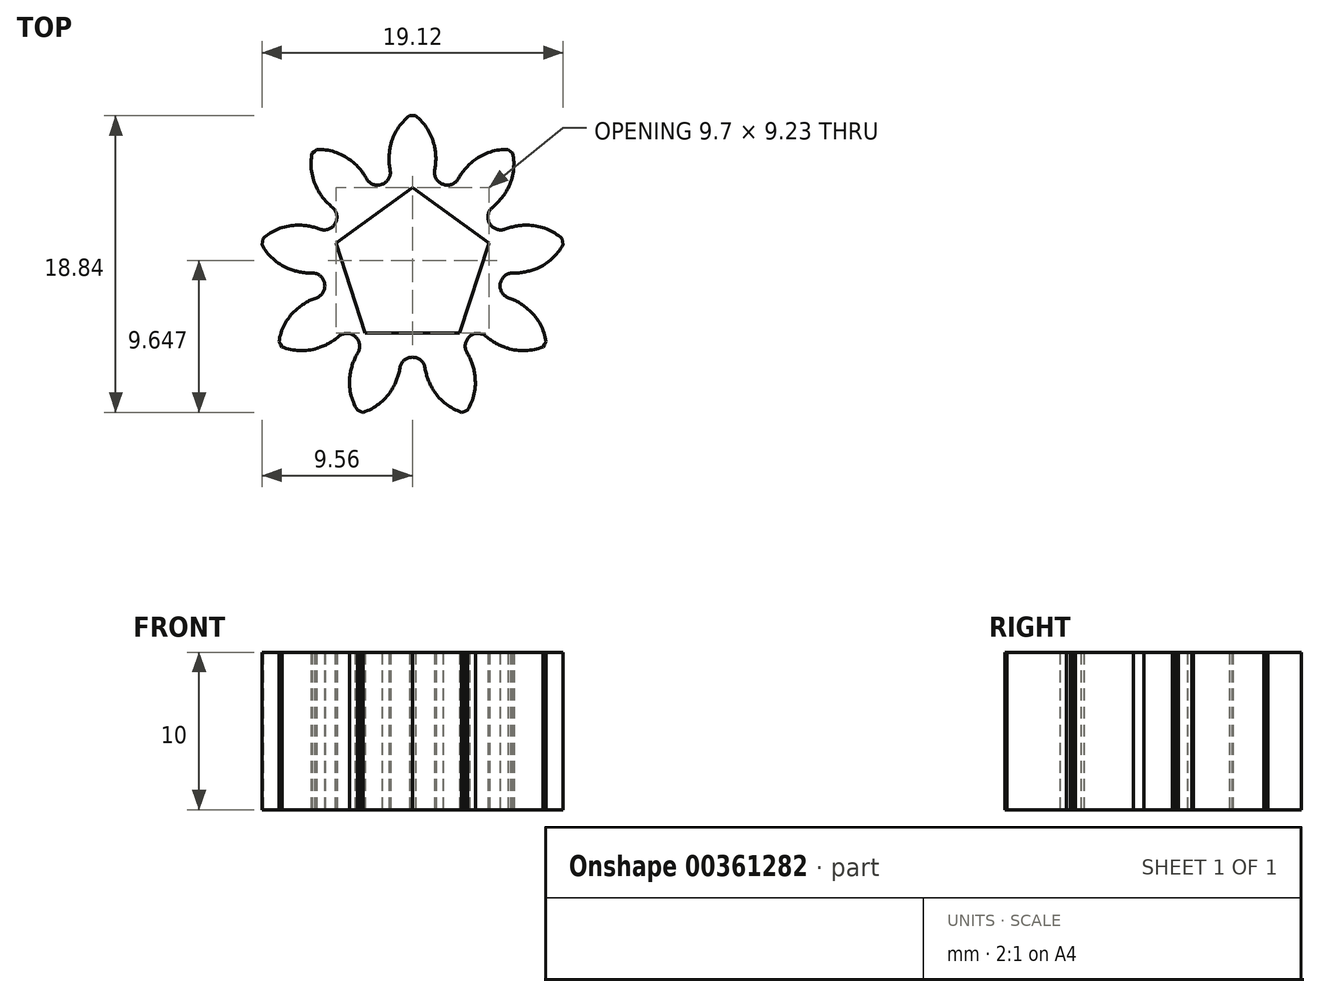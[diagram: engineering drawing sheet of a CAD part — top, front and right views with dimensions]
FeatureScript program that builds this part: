
annotation { "Feature Type Name" : "Feature", "Feature Type Description" : "" }
export const myFeature = defineFeature(function(context is Context, id is Id, definition is map)
    precondition{}
    {
        {
            var Q0;
            Q0=qCreatedBy(makeId("Top.planeOp"),FACE);
            var sketch = newSketch(context, id + "F0", { "sketchPlane" : qUnion([Q0])});
            skCircle(sketch, "E0", {"center": v(0, 0) * mm, "radius": 7.9 * mm, "construction": true});
            skCircle(sketch, "E1", {"center": v(0, 0) * mm, "radius": 9.68 * mm, "construction": true});
            skCircle(sketch, "E2", {"center": v(0, 0) * mm, "radius": 5.68 * mm, "construction": true});
            skLineSegment(sketch, "E3", {"start": v(0, 0) * mm, "end": v(0, 14.6) * mm, "construction": true});
            skLineSegment(sketch, "E4", {"start": v(0, 0) * mm, "end": v(-6.05, 14.6) * mm, "construction": true});
            skLineSegment(sketch, "E5", {"start": v(0, 0) * mm, "end": v(6.05, 14.6) * mm, "construction": true});
            skCircle(sketch, "E6", {"center": v(0, 7.9) * mm, "radius": 1.4 * mm, "construction": true});
            skCircle(sketch, "E7", {"center": v(0, 0) * mm, "radius": 7.3 * mm, "construction": true});
            skCircle(sketch, "E8", {"center": v(1.39, 7.78) * mm, "radius": 3.3 * mm, "construction": true});
            skCircle(sketch, "E9", {"center": v(1.39, 7.78) * mm, "radius": 3.77 * mm, "construction": true});
            skArc(sketch, "E10", {"start": v(1.42, 6.23) * mm, "mid": v(1.48, 7) * mm, "end": v(1.39, 7.78) * mm});
            skArc(sketch, "E11.trimOffspring", {"start": v(1.39, 7.78) * mm, "mid": v(0.96, 8.83) * mm, "end": v(0.19, 9.68) * mm});
            skLineSegment(sketch, "E12", {"start": v(2.17, 5.25) * mm, "end": v(1.96, 5.31) * mm});
            skLineSegment(sketch, "E13", {"start": v(0, 9.68) * mm, "end": v(0.19, 9.68) * mm});
            skPoint(sketch, "E14.visualSharp", {"position": v(1.22, 5.55) * mm});
            skArc(sketch, "E14.filletArc", {"start": v(1.42, 6.23) * mm, "mid": v(1.52, 5.67) * mm, "end": v(1.96, 5.31) * mm});
            skLineSegment(sketch, "E15.MirrorCS", {"start": v(-2.17, 5.25) * mm, "end": v(-1.96, 5.31) * mm});
            skLineSegment(sketch, "E16.MirrorCS", {"start": v(0, 9.68) * mm, "end": v(-0.19, 9.68) * mm});
            skArc(sketch, "E17.MirrorCS", {"start": v(-1.39, 7.78) * mm, "mid": v(-0.96, 8.83) * mm, "end": v(-0.19, 9.68) * mm});
            skArc(sketch, "E18.MirrorCS", {"start": v(-1.42, 6.23) * mm, "mid": v(-1.48, 7) * mm, "end": v(-1.39, 7.78) * mm});
            skArc(sketch, "E19.MirrorCS", {"start": v(-1.42, 6.23) * mm, "mid": v(-1.52, 5.67) * mm, "end": v(-1.96, 5.31) * mm});
            skLineSegment(sketch, "E20.1.0", {"start": v(-5.04, 2.62) * mm, "end": v(-4.92, 2.8) * mm});
            skArc(sketch, "E20.1.1", {"start": v(-5.09, 3.86) * mm, "mid": v(-4.8, 3.37) * mm, "end": v(-4.92, 2.8) * mm});
            skArc(sketch, "E20.1.2", {"start": v(-5.09, 3.86) * mm, "mid": v(-5.64, 4.41) * mm, "end": v(-6.06, 5.06) * mm});
            skArc(sketch, "E20.1.3", {"start": v(-6.06, 5.06) * mm, "mid": v(-6.4, 6.15) * mm, "end": v(-6.37, 7.3) * mm});
            skLineSegment(sketch, "E20.1.4", {"start": v(-6.22, 7.42) * mm, "end": v(-6.37, 7.3) * mm});
            skLineSegment(sketch, "E20.1.5", {"start": v(-6.22, 7.42) * mm, "end": v(-6.08, 7.54) * mm});
            skArc(sketch, "E20.1.6", {"start": v(-3.93, 6.85) * mm, "mid": v(-4.95, 7.38) * mm, "end": v(-6.08, 7.54) * mm});
            skArc(sketch, "E20.1.7", {"start": v(-2.92, 5.68) * mm, "mid": v(-3.37, 6.32) * mm, "end": v(-3.93, 6.85) * mm});
            skArc(sketch, "E20.1.8", {"start": v(-2.92, 5.68) * mm, "mid": v(-2.48, 5.32) * mm, "end": v(-1.91, 5.33) * mm});
            skLineSegment(sketch, "E20.1.9", {"start": v(-1.7, 5.42) * mm, "end": v(-1.91, 5.33) * mm});
            skLineSegment(sketch, "E20.2.0", {"start": v(-5.55, -1.23) * mm, "end": v(-5.57, -1.01) * mm});
            skArc(sketch, "E20.2.1", {"start": v(-6.38, -0.31) * mm, "mid": v(-5.84, -0.5) * mm, "end": v(-5.57, -1.01) * mm});
            skArc(sketch, "E20.2.2", {"start": v(-6.38, -0.31) * mm, "mid": v(-7.15, -0.25) * mm, "end": v(-7.9, -0.02) * mm});
            skArc(sketch, "E20.2.3", {"start": v(-7.9, -0.02) * mm, "mid": v(-8.86, 0.6) * mm, "end": v(-9.56, 1.5) * mm});
            skLineSegment(sketch, "E20.2.4", {"start": v(-9.53, 1.68) * mm, "end": v(-9.56, 1.5) * mm});
            skLineSegment(sketch, "E20.2.5", {"start": v(-9.53, 1.68) * mm, "end": v(-9.5, 1.87) * mm});
            skArc(sketch, "E20.2.6", {"start": v(-7.42, 2.72) * mm, "mid": v(-8.53, 2.48) * mm, "end": v(-9.5, 1.87) * mm});
            skArc(sketch, "E20.2.7", {"start": v(-5.89, 2.48) * mm, "mid": v(-6.64, 2.68) * mm, "end": v(-7.42, 2.72) * mm});
            skArc(sketch, "E20.2.8", {"start": v(-5.89, 2.48) * mm, "mid": v(-5.32, 2.48) * mm, "end": v(-4.9, 2.86) * mm});
            skLineSegment(sketch, "E20.2.9", {"start": v(-4.8, 3.05) * mm, "end": v(-4.9, 2.86) * mm});
            skLineSegment(sketch, "E20.3.0", {"start": v(-3.46, -4.5) * mm, "end": v(-3.62, -4.36) * mm});
            skArc(sketch, "E20.3.1", {"start": v(-4.68, -4.34) * mm, "mid": v(-4.15, -4.15) * mm, "end": v(-3.62, -4.36) * mm});
            skArc(sketch, "E20.3.2", {"start": v(-4.68, -4.34) * mm, "mid": v(-5.32, -4.79) * mm, "end": v(-6.04, -5.1) * mm});
            skArc(sketch, "E20.3.3", {"start": v(-6.04, -5.1) * mm, "mid": v(-7.17, -5.24) * mm, "end": v(-8.29, -5) * mm});
            skLineSegment(sketch, "E20.3.4", {"start": v(-8.38, -4.84) * mm, "end": v(-8.29, -5) * mm});
            skLineSegment(sketch, "E20.3.5", {"start": v(-8.38, -4.84) * mm, "end": v(-8.48, -4.68) * mm});
            skArc(sketch, "E20.3.6", {"start": v(-7.43, -2.69) * mm, "mid": v(-8.13, -3.59) * mm, "end": v(-8.48, -4.68) * mm});
            skArc(sketch, "E20.3.7", {"start": v(-6.1, -1.89) * mm, "mid": v(-6.8, -2.22) * mm, "end": v(-7.43, -2.69) * mm});
            skArc(sketch, "E20.3.8", {"start": v(-6.1, -1.89) * mm, "mid": v(-5.67, -1.52) * mm, "end": v(-5.58, -0.96) * mm});
            skLineSegment(sketch, "E20.3.9", {"start": v(-5.63, -0.74) * mm, "end": v(-5.58, -0.96) * mm});
            skLineSegment(sketch, "E20.4.0", {"start": v(0.25, -5.67) * mm, "end": v(0.03, -5.66) * mm});
            skArc(sketch, "E20.4.1", {"start": v(-0.8, -6.34) * mm, "mid": v(-0.51, -5.84) * mm, "end": v(0.03, -5.66) * mm});
            skArc(sketch, "E20.4.2", {"start": v(-0.8, -6.34) * mm, "mid": v(-1, -7.09) * mm, "end": v(-1.35, -7.78) * mm});
            skArc(sketch, "E20.4.3", {"start": v(-1.35, -7.78) * mm, "mid": v(-2.12, -8.63) * mm, "end": v(-3.13, -9.16) * mm});
            skLineSegment(sketch, "E20.4.4", {"start": v(-3.31, -9.1) * mm, "end": v(-3.13, -9.16) * mm});
            skLineSegment(sketch, "E20.4.5", {"start": v(-3.31, -9.1) * mm, "end": v(-3.49, -9.03) * mm});
            skArc(sketch, "E20.4.6", {"start": v(-3.97, -6.83) * mm, "mid": v(-3.92, -7.97) * mm, "end": v(-3.49, -9.03) * mm});
            skArc(sketch, "E20.4.7", {"start": v(-3.46, -5.37) * mm, "mid": v(-3.79, -6.07) * mm, "end": v(-3.97, -6.83) * mm});
            skArc(sketch, "E20.4.8", {"start": v(-3.46, -5.37) * mm, "mid": v(-3.36, -4.8) * mm, "end": v(-3.66, -4.32) * mm});
            skLineSegment(sketch, "E20.4.9", {"start": v(-3.84, -4.19) * mm, "end": v(-3.66, -4.32) * mm});
            skLineSegment(sketch, "E20.5.0", {"start": v(3.84, -4.19) * mm, "end": v(3.66, -4.32) * mm});
            skArc(sketch, "E20.5.1", {"start": v(3.46, -5.37) * mm, "mid": v(3.36, -4.8) * mm, "end": v(3.66, -4.32) * mm});
            skArc(sketch, "E20.5.2", {"start": v(3.46, -5.37) * mm, "mid": v(3.79, -6.07) * mm, "end": v(3.97, -6.83) * mm});
            skArc(sketch, "E20.5.3", {"start": v(3.97, -6.83) * mm, "mid": v(3.92, -7.97) * mm, "end": v(3.49, -9.03) * mm});
            skLineSegment(sketch, "E20.5.4", {"start": v(3.31, -9.1) * mm, "end": v(3.49, -9.03) * mm});
            skLineSegment(sketch, "E20.5.5", {"start": v(3.31, -9.1) * mm, "end": v(3.13, -9.16) * mm});
            skArc(sketch, "E20.5.6", {"start": v(1.35, -7.78) * mm, "mid": v(2.12, -8.63) * mm, "end": v(3.13, -9.16) * mm});
            skArc(sketch, "E20.5.7", {"start": v(0.8, -6.34) * mm, "mid": v(1, -7.09) * mm, "end": v(1.35, -7.78) * mm});
            skArc(sketch, "E20.5.8", {"start": v(0.8, -6.34) * mm, "mid": v(0.51, -5.84) * mm, "end": v(-0.03, -5.66) * mm});
            skLineSegment(sketch, "E20.5.9", {"start": v(-0.25, -5.67) * mm, "end": v(-0.03, -5.66) * mm});
            skLineSegment(sketch, "E20.6.0", {"start": v(5.63, -0.74) * mm, "end": v(5.58, -0.96) * mm});
            skArc(sketch, "E20.6.1", {"start": v(6.1, -1.89) * mm, "mid": v(5.67, -1.52) * mm, "end": v(5.58, -0.96) * mm});
            skArc(sketch, "E20.6.2", {"start": v(6.1, -1.89) * mm, "mid": v(6.8, -2.22) * mm, "end": v(7.43, -2.69) * mm});
            skArc(sketch, "E20.6.3", {"start": v(7.43, -2.69) * mm, "mid": v(8.13, -3.59) * mm, "end": v(8.48, -4.68) * mm});
            skLineSegment(sketch, "E20.6.4", {"start": v(8.38, -4.84) * mm, "end": v(8.48, -4.68) * mm});
            skLineSegment(sketch, "E20.6.5", {"start": v(8.38, -4.84) * mm, "end": v(8.29, -5) * mm});
            skArc(sketch, "E20.6.6", {"start": v(6.04, -5.1) * mm, "mid": v(7.17, -5.24) * mm, "end": v(8.29, -5) * mm});
            skArc(sketch, "E20.6.7", {"start": v(4.68, -4.34) * mm, "mid": v(5.32, -4.79) * mm, "end": v(6.04, -5.1) * mm});
            skArc(sketch, "E20.6.8", {"start": v(4.68, -4.34) * mm, "mid": v(4.15, -4.15) * mm, "end": v(3.62, -4.36) * mm});
            skLineSegment(sketch, "E20.6.9", {"start": v(3.46, -4.5) * mm, "end": v(3.62, -4.36) * mm});
            skLineSegment(sketch, "E20.7.0", {"start": v(4.8, 3.05) * mm, "end": v(4.9, 2.86) * mm});
            skArc(sketch, "E20.7.1", {"start": v(5.89, 2.48) * mm, "mid": v(5.32, 2.48) * mm, "end": v(4.9, 2.86) * mm});
            skArc(sketch, "E20.7.2", {"start": v(5.89, 2.48) * mm, "mid": v(6.64, 2.68) * mm, "end": v(7.42, 2.72) * mm});
            skArc(sketch, "E20.7.3", {"start": v(7.42, 2.72) * mm, "mid": v(8.53, 2.48) * mm, "end": v(9.5, 1.87) * mm});
            skLineSegment(sketch, "E20.7.4", {"start": v(9.53, 1.68) * mm, "end": v(9.5, 1.87) * mm});
            skLineSegment(sketch, "E20.7.5", {"start": v(9.53, 1.68) * mm, "end": v(9.56, 1.5) * mm});
            skArc(sketch, "E20.7.6", {"start": v(7.9, -0.02) * mm, "mid": v(8.86, 0.6) * mm, "end": v(9.56, 1.5) * mm});
            skArc(sketch, "E20.7.7", {"start": v(6.38, -0.31) * mm, "mid": v(7.15, -0.25) * mm, "end": v(7.9, -0.02) * mm});
            skArc(sketch, "E20.7.8", {"start": v(6.38, -0.31) * mm, "mid": v(5.84, -0.5) * mm, "end": v(5.57, -1.01) * mm});
            skLineSegment(sketch, "E20.7.9", {"start": v(5.55, -1.23) * mm, "end": v(5.57, -1.01) * mm});
            skLineSegment(sketch, "E20.8.0", {"start": v(1.7, 5.42) * mm, "end": v(1.91, 5.33) * mm});
            skArc(sketch, "E20.8.1", {"start": v(2.92, 5.68) * mm, "mid": v(2.48, 5.32) * mm, "end": v(1.91, 5.33) * mm});
            skArc(sketch, "E20.8.2", {"start": v(2.92, 5.68) * mm, "mid": v(3.37, 6.32) * mm, "end": v(3.93, 6.85) * mm});
            skArc(sketch, "E20.8.3", {"start": v(3.93, 6.85) * mm, "mid": v(4.95, 7.38) * mm, "end": v(6.08, 7.54) * mm});
            skLineSegment(sketch, "E20.8.4", {"start": v(6.22, 7.42) * mm, "end": v(6.08, 7.54) * mm});
            skLineSegment(sketch, "E20.8.5", {"start": v(6.22, 7.42) * mm, "end": v(6.37, 7.3) * mm});
            skArc(sketch, "E20.8.6", {"start": v(6.06, 5.06) * mm, "mid": v(6.4, 6.15) * mm, "end": v(6.37, 7.3) * mm});
            skArc(sketch, "E20.8.7", {"start": v(5.09, 3.86) * mm, "mid": v(5.64, 4.41) * mm, "end": v(6.06, 5.06) * mm});
            skArc(sketch, "E20.8.8", {"start": v(5.09, 3.86) * mm, "mid": v(4.8, 3.37) * mm, "end": v(4.92, 2.8) * mm});
            skLineSegment(sketch, "E20.8.9", {"start": v(5.04, 2.62) * mm, "end": v(4.92, 2.8) * mm});
            skCircle(sketch, "E21.cCircle", {"center": v(0, 0) * mm, "radius": 4.13 * mm, "construction": true});
            skLineSegment(sketch, "E21.0", {"start": v(4.85, 1.58) * mm, "end": v(3, -4.13) * mm});
            skLineSegment(sketch, "E21.1", {"start": v(3, -4.13) * mm, "end": v(-3, -4.13) * mm});
            skLineSegment(sketch, "E21.2", {"start": v(-3, -4.13) * mm, "end": v(-4.85, 1.58) * mm});
            skLineSegment(sketch, "E21.3", {"start": v(-4.85, 1.58) * mm, "end": v(0, 5.1) * mm});
            skLineSegment(sketch, "E21.4", {"start": v(0, 5.1) * mm, "end": v(4.85, 1.58) * mm});
            skSolve(sketch);
        }
        {
            var Q0;
            {var subQ32=sQuery(id+"F0.wireOp",EDGE,"E10");Q0=makeQuery(id+"F0.imprint","IMPRINT",FACE,{"disambiguationData":[TD([[makeQuery(id+"F0.imprint","IMPRINT",EDGE,{"derivedFrom":subQ32}),1.0]])]});}
            extrude(context, id + "F1", {"entities" : qUnion([Q0]), "depth" : 10 * mm});
        }
    });
